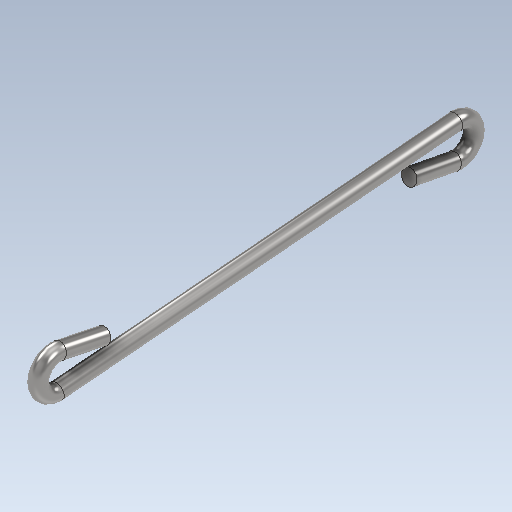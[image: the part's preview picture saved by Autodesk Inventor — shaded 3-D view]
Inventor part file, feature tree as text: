
AUTODESK INVENTOR PART (.ipt)
format: ipt  version: 2021 (Build 250183000, 183)  size: 159,232 bytes
history: native  units: mm
features: sketch x2, other x1, sweep x1
ambient origin geometry x8: Origin, YZ Plane, XZ Plane, XY Plane, X Axis, Y Axis, Z Axis, Center Point
bodies: Body1 (feature_tree)
feature tree (4):
  other  "Sólido1"
  sweep  "Barrido1"
  sketch  "Boceto1"  dims[d0=2.8mm d11=6.9mm]
  sketch  "Boceto2"  dims[d12=60.0mm d13=2.3mm d14=1.15mm d15=6.9mm d18=2.55mm d19=2.3mm d20=0.0mm d21=0.0mm d22=1.4mm d23=0.0mm d25=1.15mm d26=1.15mm]
